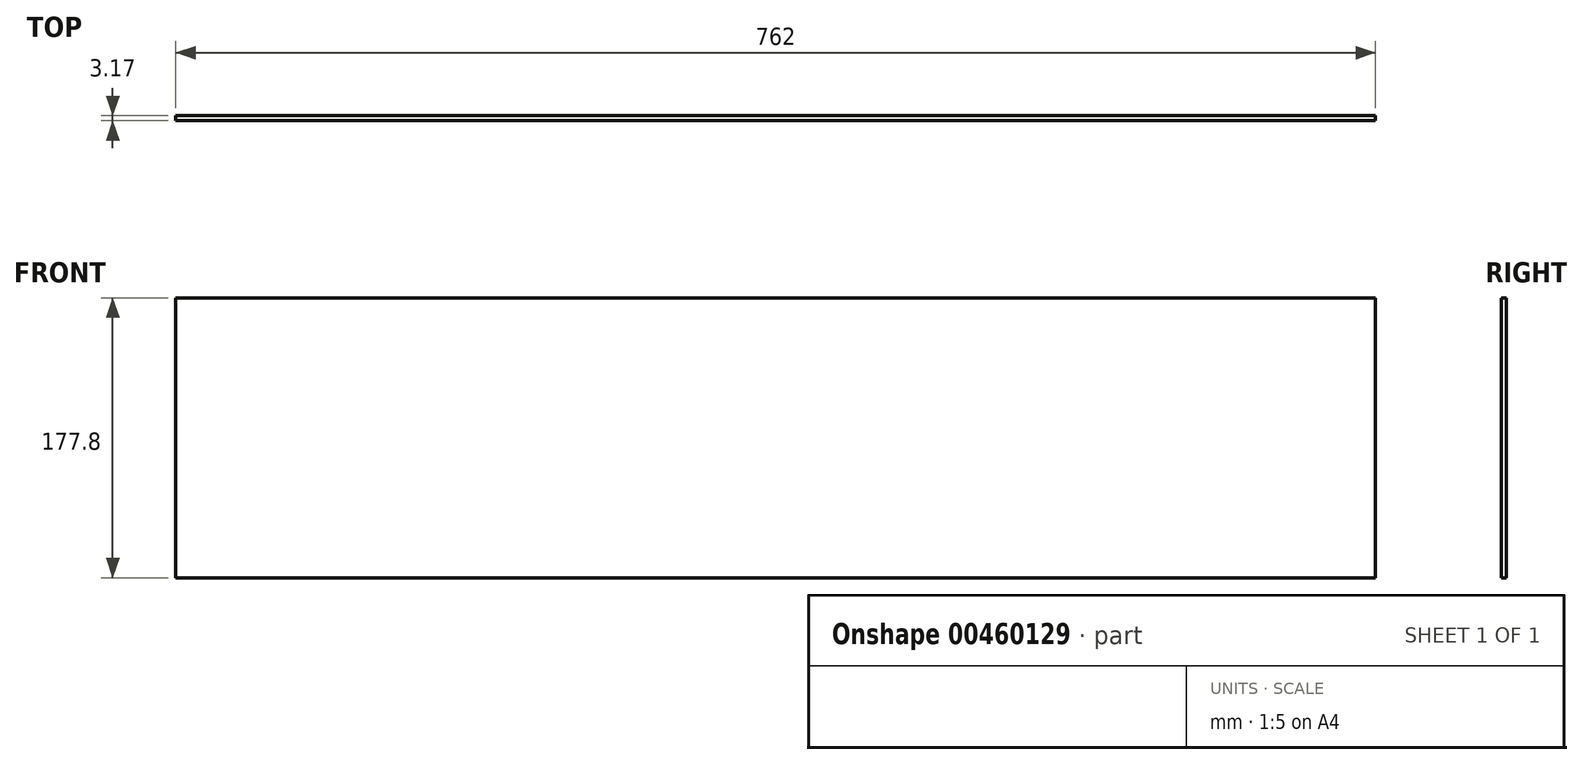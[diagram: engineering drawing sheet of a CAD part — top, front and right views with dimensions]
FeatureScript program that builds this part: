
annotation { "Feature Type Name" : "Feature", "Feature Type Description" : "" }
export const myFeature = defineFeature(function(context is Context, id is Id, definition is map)
    precondition{}
    {
        {
            var Q0;
            Q0=qCreatedBy(makeId("Front.planeOp"),FACE);
            var sketch = newSketch(context, id + "F0", { "sketchPlane" : qUnion([Q0])});
            skLineSegment(sketch, "E0.bottom", {"start": v(-391.47, 73.22) * mm, "end": v(370.53, 73.22) * mm});
            skLineSegment(sketch, "E0.top", {"start": v(-391.47, -104.58) * mm, "end": v(370.53, -104.58) * mm});
            skLineSegment(sketch, "E0.left", {"start": v(-391.47, 73.22) * mm, "end": v(-391.47, -104.58) * mm});
            skLineSegment(sketch, "E0.right", {"start": v(370.53, 73.22) * mm, "end": v(370.53, -104.58) * mm});
            skSolve(sketch);
        }
        {
            var Q0;
            Q0=makeQuery(id+"F0.imprint","IMPRINT",FACE,{"disambiguationData":[TD([[makeQuery(id+"F0.imprint","IMPRINT",EDGE,{"derivedFrom":sQuery(id+"F0.wireOp",EDGE,"E0.bottom")}),-1.0]])]});
            extrude(context, id + "F1", {"entities" : qUnion([Q0]), "depth" : 3.17 * mm});
        }
    });
